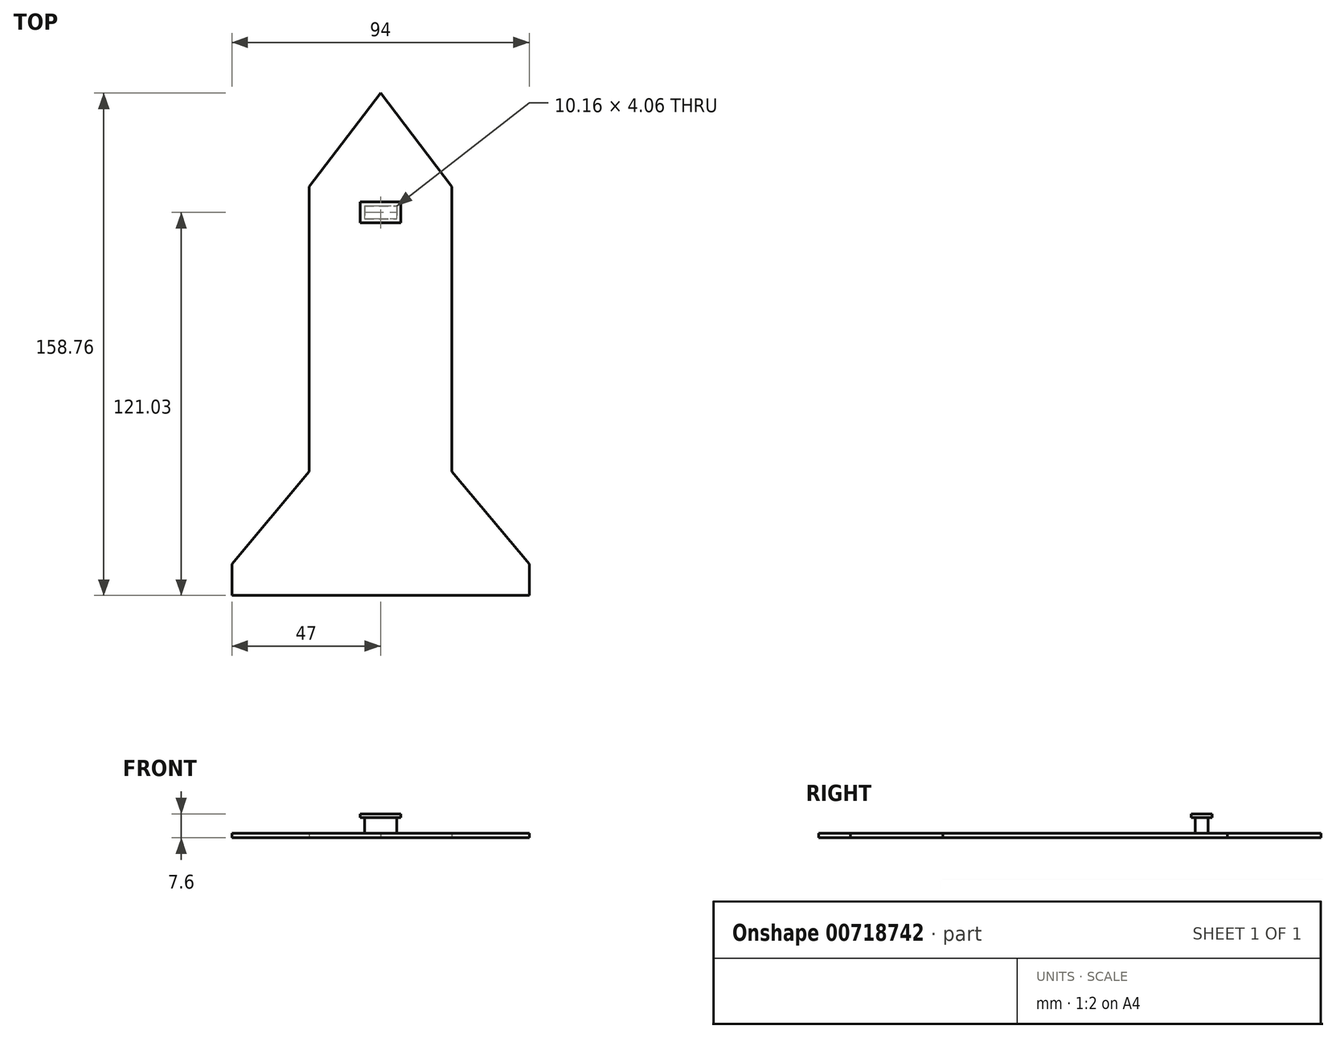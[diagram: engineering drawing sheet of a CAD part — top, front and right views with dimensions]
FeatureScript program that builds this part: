
annotation { "Feature Type Name" : "Feature", "Feature Type Description" : "" }
export const myFeature = defineFeature(function(context is Context, id is Id, definition is map)
    precondition{}
    {
        {
            var Q0;
            Q0=qCreatedBy(makeId("Top.planeOp"),FACE);
            var sketch = newSketch(context, id + "F0", { "sketchPlane" : qUnion([Q0])});
            skLineSegment(sketch, "E0.top", {"start": v(-39.32, -13.3) * mm, "end": v(54.68, -13.3) * mm});
            skLineSegment(sketch, "E0.left", {"start": v(-39.32, -3.3) * mm, "end": v(-39.32, -13.3) * mm});
            skLineSegment(sketch, "E0.right", {"start": v(54.68, -3.3) * mm, "end": v(54.68, -13.3) * mm});
            skPoint(sketch, "E1", {"position": v(7.68, -13.3) * mm});
            skPoint(sketch, "E2", {"position": v(7.68, 71.01) * mm});
            skLineSegment(sketch, "E3", {"start": v(-39.32, -3.3) * mm, "end": v(-14.83, 25.9) * mm});
            skLineSegment(sketch, "E4", {"start": v(54.68, -3.3) * mm, "end": v(30.19, 25.9) * mm});
            skLineSegment(sketch, "E5", {"start": v(-14.83, 25.9) * mm, "end": v(-14.83, 115.9) * mm});
            skLineSegment(sketch, "E6", {"start": v(30.19, 25.9) * mm, "end": v(30.19, 115.9) * mm});
            skLineSegment(sketch, "E7", {"start": v(7.68, 145.47) * mm, "end": v(-14.83, 115.9) * mm});
            skLineSegment(sketch, "E8", {"start": v(30.19, 115.9) * mm, "end": v(7.68, 145.47) * mm});
            skSolve(sketch);
        }
        {
            var Q0;
            Q0=makeQuery(id+"F0.imprint","IMPRINT",FACE,{"disambiguationData":[TD([[makeQuery(id+"F0.imprint","IMPRINT",EDGE,{"derivedFrom":sQuery(id+"F0.wireOp",EDGE,"E0.top")}),1.0]])]});
            var Q1;
            Q1 = qSketchRegion(id + "F0", true);
            extrude(context, id + "F1", {"entities" : qUnion([Q0, Q1]), "depth" : 1.4 * mm, "offsetDistance" : 25.4 * mm});
        }
        {
            var Q0;
            Q0=makeQuery(id+"F1.opExtrude","CAP_FACE",FACE,{"disambiguationData":[OSD([sQuery(id+"F0.wireOp",EDGE,"E0.top"),sQuery(id+"F0.wireOp",EDGE,"E0.left"),sQuery(id+"F0.wireOp",EDGE,"E0.right"),sQuery(id+"F0.wireOp",EDGE,"E3"),sQuery(id+"F0.wireOp",EDGE,"E4"),sQuery(id+"F0.wireOp",EDGE,"E5"),sQuery(id+"F0.wireOp",EDGE,"E6"),sQuery(id+"F0.wireOp",EDGE,"E7"),sQuery(id+"F0.wireOp",EDGE,"E8")])],"isStart":false});
            var sketch = newSketch(context, id + "F2", { "sketchPlane" : qUnion([Q0])});
            skPoint(sketch, "E9", {"position": v(7.68, -13.3) * mm});
            skPoint(sketch, "E10", {"position": v(7.68, 129.4) * mm});
            skLineSegment(sketch, "E11.bottom", {"start": v(2.6, 109.77) * mm, "end": v(12.76, 109.77) * mm});
            skLineSegment(sketch, "E11.top", {"start": v(2.6, 105.7) * mm, "end": v(12.76, 105.7) * mm});
            skLineSegment(sketch, "E11.left", {"start": v(2.6, 109.77) * mm, "end": v(2.6, 105.7) * mm});
            skLineSegment(sketch, "E11.right", {"start": v(12.76, 109.77) * mm, "end": v(12.76, 105.7) * mm});
            skPoint(sketch, "E12", {"position": v(7.68, 109.77) * mm});
            skSolve(sketch);
        }
        {
            var Q0;
            Q0 = qSketchRegion(id + "F2", true);
            extrude(context, id + "F3", {"entities" : qUnion([Q0]), "operationType" : NewBodyOperationType.ADD, "depth" : 5 * mm, "offsetDistance" : 25.4 * mm});
        }
        {
            var Q0;
            Q0=makeQuery(id+"F3.opExtrude","CAP_FACE",FACE,{"disambiguationData":[OSD([sQuery(id+"F2.wireOp",EDGE,"E11.bottom"),sQuery(id+"F2.wireOp",EDGE,"E11.top"),sQuery(id+"F2.wireOp",EDGE,"E11.left"),sQuery(id+"F2.wireOp",EDGE,"E11.right")])],"isStart":false});
            var sketch = newSketch(context, id + "F4", { "sketchPlane" : qUnion([Q0])});
            skLineSegment(sketch, "E13.0", {"start": v(1.3, 111.07) * mm, "end": v(14.06, 111.07) * mm});
            skLineSegment(sketch, "E13.1", {"start": v(1.3, 111.07) * mm, "end": v(1.3, 104.4) * mm});
            skLineSegment(sketch, "E13.2", {"start": v(1.3, 104.4) * mm, "end": v(14.06, 104.4) * mm});
            skLineSegment(sketch, "E13.3", {"start": v(14.06, 111.07) * mm, "end": v(14.06, 104.4) * mm});
            skSolve(sketch);
        }
        {
            var Q0;
            Q0 = qSketchRegion(id + "F4", true);
            extrude(context, id + "F5", {"entities" : qUnion([Q0]), "operationType" : NewBodyOperationType.ADD, "depth" : 1.2 * mm, "offsetDistance" : 25.4 * mm});
        }
    });
